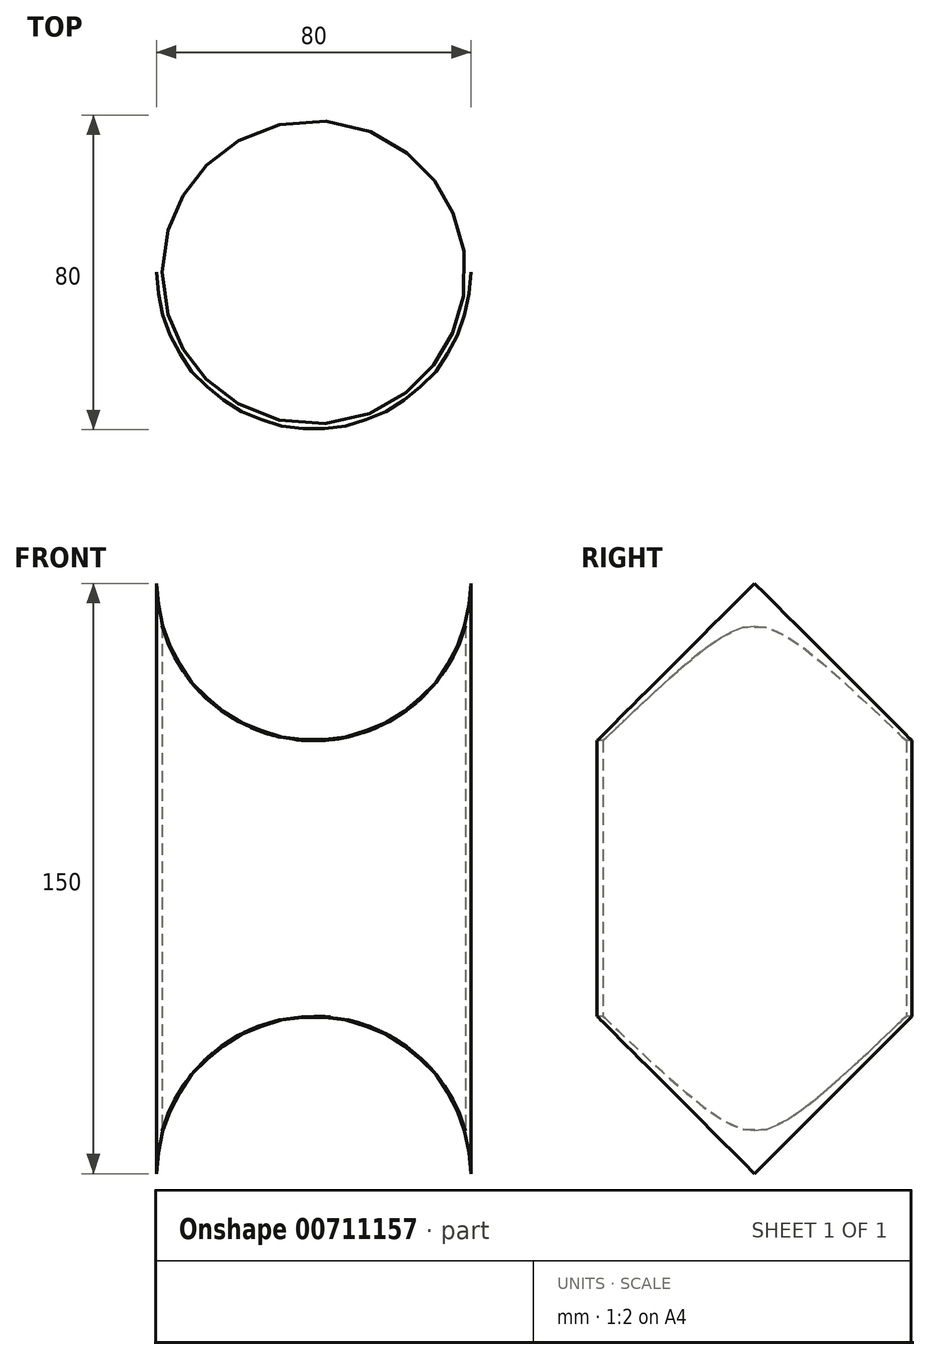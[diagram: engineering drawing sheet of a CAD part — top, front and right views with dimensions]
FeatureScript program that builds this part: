
annotation { "Feature Type Name" : "Feature", "Feature Type Description" : "" }
export const myFeature = defineFeature(function(context is Context, id is Id, definition is map)
    precondition{}
    {
        {
            var Q0;
            Q0=qCreatedBy(makeId("Top.planeOp"),FACE);
            var sketch = newSketch(context, id + "F0", { "sketchPlane" : qUnion([Q0])});
            skCircle(sketch, "E0", {"center": v(0, 0) * mm, "radius": 40 * mm});
            skCircle(sketch, "E1", {"center": v(0, 0) * mm, "radius": 38.5 * mm});
            skSolve(sketch);
        }
        {
            var Q0;
            Q0 = qSketchRegion(id + "F0", true);
            extrude(context, id + "F1", {"entities" : qUnion([Q0]), "endBound" : BoundingType.SYMMETRIC, "depth" : 150 * mm, "offsetDistance" : 25 * mm});
        }
        {
            var Q0;
            Q0=qCreatedBy(makeId("Front.planeOp"),FACE);
            var sketch = newSketch(context, id + "F2", { "sketchPlane" : qUnion([Q0])});
            skCircle(sketch, "E2", {"center": v(0, 75) * mm, "radius": 40 * mm});
            skCircle(sketch, "E3", {"center": v(0, -75) * mm, "radius": 40 * mm});
            skLineSegment(sketch, "E4", {"start": v(0, 75) * mm, "end": v(0, -75) * mm, "construction": true});
            skSolve(sketch);
        }
        {
            var Q0;
            Q0 = qSketchRegion(id + "F2", true);
            extrude(context, id + "F3", {"entities" : qUnion([Q0]), "operationType" : NewBodyOperationType.REMOVE, "endBound" : BoundingType.THROUGH_ALL, "oppositeDirection" : true, "depth" : 25 * mm, "offsetDistance" : 25 * mm, "hasSecondDirection" : true, "secondDirectionBound" : SecondDirectionBoundingType.THROUGH_ALL, "secondDirectionOppositeDirection" : false, "secondDirectionDepth" : 25 * mm});
        }
    });
